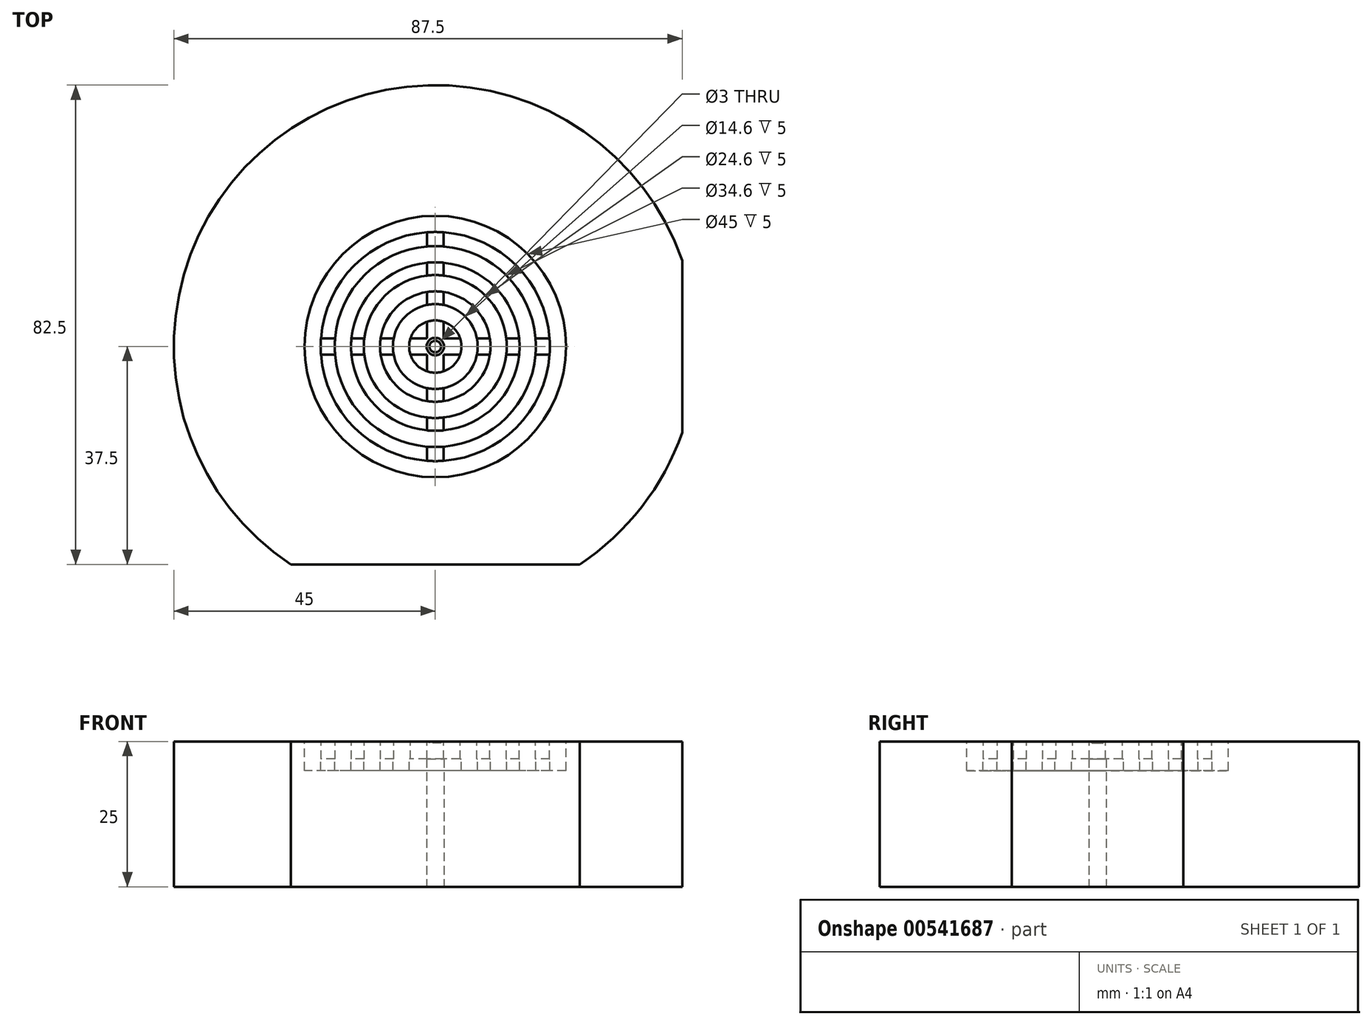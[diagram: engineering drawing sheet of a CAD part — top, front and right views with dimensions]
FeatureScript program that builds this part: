
annotation { "Feature Type Name" : "Feature", "Feature Type Description" : "" }
export const myFeature = defineFeature(function(context is Context, id is Id, definition is map)
    precondition{}
    {
        {
            var Q0;
            Q0=qCreatedBy(makeId("Top.planeOp"),FACE);
            var sketch = newSketch(context, id + "F0", { "sketchPlane" : qUnion([Q0])});
            skCircle(sketch, "E0", {"center": v(0, 0) * mm, "radius": 45 * mm});
            skCircle(sketch, "E1", {"center": v(0, 0) * mm, "radius": 1.5 * mm});
            skSolve(sketch);
        }
        {
            var Q0;
            Q0 = qSketchRegion(id + "F0", true);
            extrude(context, id + "F1", {"entities" : qUnion([Q0]), "depth" : 25 * mm, "offsetDistance" : 25 * mm});
        }
        {
            var Q0;
            Q0=makeQuery(id+"F1.opExtrude","CAP_FACE",FACE,{"disambiguationData":[OSD([sQuery(id+"F0.wireOp",EDGE,"E0")])],"isStart":false});
            var sketch = newSketch(context, id + "F2", { "sketchPlane" : qUnion([Q0])});
            skCircle(sketch, "E2", {"center": v(0, 0) * mm, "radius": 22.5 * mm});
            skCircle(sketch, "E3.0", {"center": v(0, 0) * mm, "radius": 19.72 * mm});
            skCircle(sketch, "E4", {"center": v(0, 0) * mm, "radius": 18.5 * mm});
            skCircle(sketch, "E5.0", {"center": v(0, 0) * mm, "radius": 15.72 * mm});
            skCircle(sketch, "E6", {"center": v(0, 0) * mm, "radius": 14 * mm});
            skCircle(sketch, "E7", {"center": v(0, 0) * mm, "radius": 10 * mm});
            skCircle(sketch, "E8.0", {"center": v(0, 0) * mm, "radius": 7.22 * mm});
            skCircle(sketch, "E9.0", {"center": v(0, 0) * mm, "radius": 11.22 * mm});
            skLineSegment(sketch, "E10", {"start": v(-1, 22.48) * mm, "end": v(-1, 7.15) * mm});
            skLineSegment(sketch, "E11", {"start": v(1.39, 22.46) * mm, "end": v(1.4, -7.08) * mm});
            skLineSegment(sketch, "E12", {"start": v(0, 7.22) * mm, "end": v(0, 22.5) * mm, "construction": true});
            skLineSegment(sketch, "E13.1.0", {"start": v(-16.4, 15.1) * mm, "end": v(-5.57, 4.27) * mm});
            skLineSegment(sketch, "E13.1.1", {"start": v(-14.7, 16.78) * mm, "end": v(6.19, -4.1) * mm});
            skLineSegment(sketch, "E13.2.0", {"start": v(-22.09, -1) * mm, "end": v(-6.76, -1) * mm});
            skLineSegment(sketch, "E13.2.1", {"start": v(-22.07, 1.4) * mm, "end": v(7.47, 1.4) * mm});
            skPoint(sketch, "E13.center", {"position": v(0.2, 0.2) * mm});
            skLineSegment(sketch, "E14.2.3.0", {"start": v(-14.72, -16.4) * mm, "end": v(-3.88, -5.57) * mm});
            skLineSegment(sketch, "E14.3.3.0", {"start": v(-16.4, -14.7) * mm, "end": v(4.5, 6.19) * mm});
            skLineSegment(sketch, "E15.2.4.0", {"start": v(1.4, -22.09) * mm, "end": v(1.39, -6.76) * mm});
            skLineSegment(sketch, "E15.3.4.0", {"start": v(-1, -22.07) * mm, "end": v(-1, 7.47) * mm});
            skLineSegment(sketch, "E15.2.5.0", {"start": v(16.8, -14.72) * mm, "end": v(5.96, -3.88) * mm});
            skLineSegment(sketch, "E15.3.5.0", {"start": v(15.1, -16.4) * mm, "end": v(-5.8, 4.5) * mm});
            skLineSegment(sketch, "E15.2.6.0", {"start": v(22.48, 1.4) * mm, "end": v(7.15, 1.4) * mm});
            skLineSegment(sketch, "E15.3.6.0", {"start": v(22.46, -1) * mm, "end": v(-7.08, -1) * mm});
            skLineSegment(sketch, "E15.2.7.0", {"start": v(15.1, 16.8) * mm, "end": v(4.27, 5.96) * mm});
            skLineSegment(sketch, "E15.3.7.0", {"start": v(16.78, 15.1) * mm, "end": v(-4.1, -5.8) * mm});
            skLineSegment(sketch, "E16", {"start": v(7.15, 1.4) * mm, "end": v(7.47, 1.4) * mm});
            skLineSegment(sketch, "E17", {"start": v(-7.08, -1) * mm, "end": v(-6.76, -1) * mm});
            skLineSegment(sketch, "E18", {"start": v(1.4, -6.76) * mm, "end": v(1.4, -7.08) * mm});
            skLineSegment(sketch, "E19", {"start": v(-1, 7.47) * mm, "end": v(-1, 7.15) * mm});
            skSolve(sketch);
        }
        {
            var Q0;
            Q0 = qSketchRegion(id + "F2", true);
            extrude(context, id + "F3", {"entities" : qUnion([Q0]), "operationType" : NewBodyOperationType.REMOVE, "oppositeDirection" : true, "depth" : 5 * mm, "offsetDistance" : 25 * mm});
        }
        {
            var Q0;
            {var subQ0=sQuery(id+"F0.wireOp",EDGE,"E1");Q0=makeQuery(id+"F3.boolean.opBoolean","SPLIT",FACE,{"disambiguationData":[TD([makeQuery(id+"F1.opExtrude","SWEPT_FACE",FACE,{"disambiguationData":[OSD([subQ0])]})])],"derivedFrom":makeQuery(id+"F1.opExtrude","CAP_FACE",FACE,{"disambiguationData":[OSD([sQuery(id+"F0.wireOp",EDGE,"E0"),subQ0])],"isStart":false})});}
            var sketch = newSketch(context, id + "F4", { "sketchPlane" : qUnion([Q0])});
            skCircle(sketch, "E20", {"center": v(0, 0) * mm, "radius": 4.5 * mm});
            skCircle(sketch, "E21", {"center": v(0, 0) * mm, "radius": 7.3 * mm});
            skSolve(sketch);
        }
        {
            var Q0;
            Q0=makeQuery(id+"F4.imprint","IMPRINT",FACE,{"disambiguationData":[TD([[makeQuery(id+"F4.imprint","IMPRINT",EDGE,{"derivedFrom":sQuery(id+"F4.wireOp",EDGE,"E20")}),-1.0]])]});
            extrude(context, id + "F5", {"entities" : qUnion([Q0]), "operationType" : NewBodyOperationType.REMOVE, "oppositeDirection" : true, "depth" : 5 * mm, "offsetDistance" : 25 * mm});
        }
        {
            var Q0;
            {var subQ0=makeQuery(id+"F3.opExtrude","SWEPT_FACE",FACE,{"disambiguationData":[OSD([sQuery(id+"F2.wireOp",EDGE,"E3.0")])]});var subQ1=sQuery(id+"F0.wireOp",EDGE,"E1");Q0=makeQuery(id+"F5.boolean.opBoolean","SPLIT",FACE,{"disambiguationData":[TD([makeQuery(id+"F3.boolean.opBoolean","COPY",FACE,{"derivedFrom":subQ0})])],"derivedFrom":makeQuery(id+"F3.boolean.opBoolean","SPLIT",FACE,{"disambiguationData":[TD([makeQuery(id+"F1.opExtrude","SWEPT_FACE",FACE,{"disambiguationData":[OSD([subQ1])]})])],"derivedFrom":makeQuery(id+"F1.opExtrude","CAP_FACE",FACE,{"disambiguationData":[OSD([sQuery(id+"F0.wireOp",EDGE,"E0"),subQ1])],"isStart":false})})});}
            var sketch = newSketch(context, id + "F6", { "sketchPlane" : qUnion([Q0])});
            skCircle(sketch, "E22", {"center": v(0, 0) * mm, "radius": 9.5 * mm});
            skCircle(sketch, "E23", {"center": v(0, 0) * mm, "radius": 12.3 * mm});
            skSolve(sketch);
        }
        {
            var Q0;
            Q0=makeQuery(id+"F6.imprint","IMPRINT",FACE,{"disambiguationData":[TD([[makeQuery(id+"F6.imprint","IMPRINT",EDGE,{"derivedFrom":sQuery(id+"F6.wireOp",EDGE,"E22")}),-1.0]])]});
            extrude(context, id + "F7", {"entities" : qUnion([Q0]), "operationType" : NewBodyOperationType.REMOVE, "oppositeDirection" : true, "depth" : 5 * mm, "offsetDistance" : 25 * mm});
        }
        {
            var Q0;
            {var subQ0=makeQuery(id+"F3.opExtrude","SWEPT_FACE",FACE,{"disambiguationData":[OSD([sQuery(id+"F2.wireOp",EDGE,"E3.0")])]});var subQ1=makeQuery(id+"F3.boolean.opBoolean","COPY",FACE,{"derivedFrom":subQ0});var subQ2=sQuery(id+"F0.wireOp",EDGE,"E1");Q0=makeQuery(id+"F7.boolean.opBoolean","SPLIT",FACE,{"disambiguationData":[TD([subQ1])],"derivedFrom":makeQuery(id+"F5.boolean.opBoolean","SPLIT",FACE,{"disambiguationData":[TD([subQ1])],"derivedFrom":makeQuery(id+"F3.boolean.opBoolean","SPLIT",FACE,{"disambiguationData":[TD([makeQuery(id+"F1.opExtrude","SWEPT_FACE",FACE,{"disambiguationData":[OSD([subQ2])]})])],"derivedFrom":makeQuery(id+"F1.opExtrude","CAP_FACE",FACE,{"disambiguationData":[OSD([sQuery(id+"F0.wireOp",EDGE,"E0"),subQ2])],"isStart":false})})})});}
            var sketch = newSketch(context, id + "F8", { "sketchPlane" : qUnion([Q0])});
            skCircle(sketch, "E24", {"center": v(0, 0) * mm, "radius": 14.5 * mm});
            skCircle(sketch, "E25", {"center": v(0, 0) * mm, "radius": 17.3 * mm});
            skSolve(sketch);
        }
        {
            var Q0;
            Q0=makeQuery(id+"F8.imprint","IMPRINT",FACE,{"disambiguationData":[TD([[makeQuery(id+"F8.imprint","IMPRINT",EDGE,{"derivedFrom":sQuery(id+"F8.wireOp",EDGE,"E24")}),-1.0]])]});
            extrude(context, id + "F9", {"entities" : qUnion([Q0]), "operationType" : NewBodyOperationType.REMOVE, "oppositeDirection" : true, "depth" : 5 * mm, "offsetDistance" : 25 * mm});
        }
        {
            var Q0;
            {var subQ0=sQuery(id+"F0.wireOp",EDGE,"E0");Q0=makeQuery(id+"F3.boolean.opBoolean","SPLIT",FACE,{"disambiguationData":[TD([makeQuery(id+"F1.opExtrude","SWEPT_FACE",FACE,{"disambiguationData":[OSD([subQ0])]})])],"derivedFrom":makeQuery(id+"F1.opExtrude","CAP_FACE",FACE,{"disambiguationData":[OSD([subQ0,sQuery(id+"F0.wireOp",EDGE,"E1")])],"isStart":false})});}
            var sketch = newSketch(context, id + "F10", { "sketchPlane" : qUnion([Q0])});
            skLineSegment(sketch, "E26.bottom", {"start": v(1.4, 20.35) * mm, "end": v(-1.4, 20.35) * mm});
            skLineSegment(sketch, "E26.top", {"start": v(1.4, -20.35) * mm, "end": v(-1.4, -20.35) * mm});
            skLineSegment(sketch, "E26.left", {"start": v(1.4, 20.35) * mm, "end": v(1.4, -20.35) * mm});
            skLineSegment(sketch, "E26.right", {"start": v(-1.4, 20.35) * mm, "end": v(-1.4, -20.35) * mm});
            skPoint(sketch, "E26.middle", {"position": v(0, 0) * mm});
            skSolve(sketch);
        }
        {
            var Q0;
            Q0=makeQuery(id+"F10.imprint","IMPRINT",FACE,{"disambiguationData":[TD([[makeQuery(id+"F10.imprint","IMPRINT",EDGE,{"derivedFrom":makeQuery(id+"F1.opExtrude","CAP_EDGE",EDGE,{"disambiguationData":[OSD([sQuery(id+"F0.wireOp",EDGE,"E0")])],"isStart":false})}),1.0]])]});
            var sketch = newSketch(context, id + "F11", { "sketchPlane" : qUnion([Q0])});
            skLineSegment(sketch, "E27.bottom", {"start": v(20.75, -1.4) * mm, "end": v(-20.75, -1.4) * mm});
            skLineSegment(sketch, "E27.top", {"start": v(20.75, 1.4) * mm, "end": v(-20.75, 1.4) * mm});
            skLineSegment(sketch, "E27.left", {"start": v(20.75, -1.4) * mm, "end": v(20.75, 1.4) * mm});
            skLineSegment(sketch, "E27.right", {"start": v(-20.75, -1.4) * mm, "end": v(-20.75, 1.4) * mm});
            skPoint(sketch, "E27.middle", {"position": v(0, 0) * mm});
            skSolve(sketch);
        }
        {
            var Q0;
            Q0 = qSketchRegion(id + "F10", true);
            var Q1;
            Q1 = qSketchRegion(id + "F11", true);
            extrude(context, id + "F12", {"entities" : qUnion([Q0, Q1]), "operationType" : NewBodyOperationType.REMOVE, "oppositeDirection" : true, "depth" : 3 * mm, "offsetDistance" : 25 * mm});
        }
        {
            var Q0;
            {var subQ0=sQuery(id+"F0.wireOp",EDGE,"E0");Q0=makeQuery(id+"F3.boolean.opBoolean","SPLIT",FACE,{"disambiguationData":[TD([makeQuery(id+"F1.opExtrude","SWEPT_FACE",FACE,{"disambiguationData":[OSD([subQ0])]})])],"derivedFrom":makeQuery(id+"F1.opExtrude","CAP_FACE",FACE,{"disambiguationData":[OSD([subQ0,sQuery(id+"F0.wireOp",EDGE,"E1")])],"isStart":false})});}
            var sketch = newSketch(context, id + "F13", { "sketchPlane" : qUnion([Q0])});
            skLineSegment(sketch, "E28.bottom", {"start": v(27.5, -52.5) * mm, "end": v(-27.5, -52.5) * mm});
            skLineSegment(sketch, "E28.top", {"start": v(27.5, -37.5) * mm, "end": v(-27.5, -37.5) * mm});
            skLineSegment(sketch, "E28.left", {"start": v(27.5, -52.5) * mm, "end": v(27.5, -37.5) * mm});
            skLineSegment(sketch, "E28.right", {"start": v(-27.5, -52.5) * mm, "end": v(-27.5, -37.5) * mm});
            skPoint(sketch, "E28.middle", {"position": v(0, -45) * mm});
            skLineSegment(sketch, "E29.bottom", {"start": v(47.5, -15) * mm, "end": v(42.5, -15) * mm});
            skLineSegment(sketch, "E29.top", {"start": v(47.5, 15) * mm, "end": v(42.5, 15) * mm});
            skLineSegment(sketch, "E29.left", {"start": v(47.5, -15) * mm, "end": v(47.5, 15) * mm});
            skLineSegment(sketch, "E29.right", {"start": v(42.5, -15) * mm, "end": v(42.5, 15) * mm});
            skPoint(sketch, "E29.middle", {"position": v(45, 0) * mm});
            skSolve(sketch);
        }
        {
            var Q0;
            Q0 = qSketchRegion(id + "F13", true);
            extrude(context, id + "F14", {"entities" : qUnion([Q0]), "operationType" : NewBodyOperationType.REMOVE, "oppositeDirection" : true, "depth" : 25 * mm, "offsetDistance" : 25 * mm});
        }
        {
            var Q0;
            {var subQ0=sQuery(id+"F0.wireOp",EDGE,"E0");Q0=makeQuery(id+"F3.boolean.opBoolean","SPLIT",FACE,{"disambiguationData":[TD([makeQuery(id+"F1.opExtrude","SWEPT_FACE",FACE,{"disambiguationData":[OSD([subQ0])]})])],"derivedFrom":makeQuery(id+"F1.opExtrude","CAP_FACE",FACE,{"disambiguationData":[OSD([subQ0,sQuery(id+"F0.wireOp",EDGE,"E1")])],"isStart":false})});}
            var sketch = newSketch(context, id + "F15", { "sketchPlane" : qUnion([Q0])});
            skCircle(sketch, "E30", {"center": v(0, 0) * mm, "radius": 1 * mm});
            skSolve(sketch);
        }
        {
            var Q0;
            Q0 = qSketchRegion(id + "F15", true);
            extrude(context, id + "F16", {"entities" : qUnion([Q0]), "oppositeDirection" : true, "depth" : .25 * mm, "offsetDistance" : 25 * mm});
        }
    });
